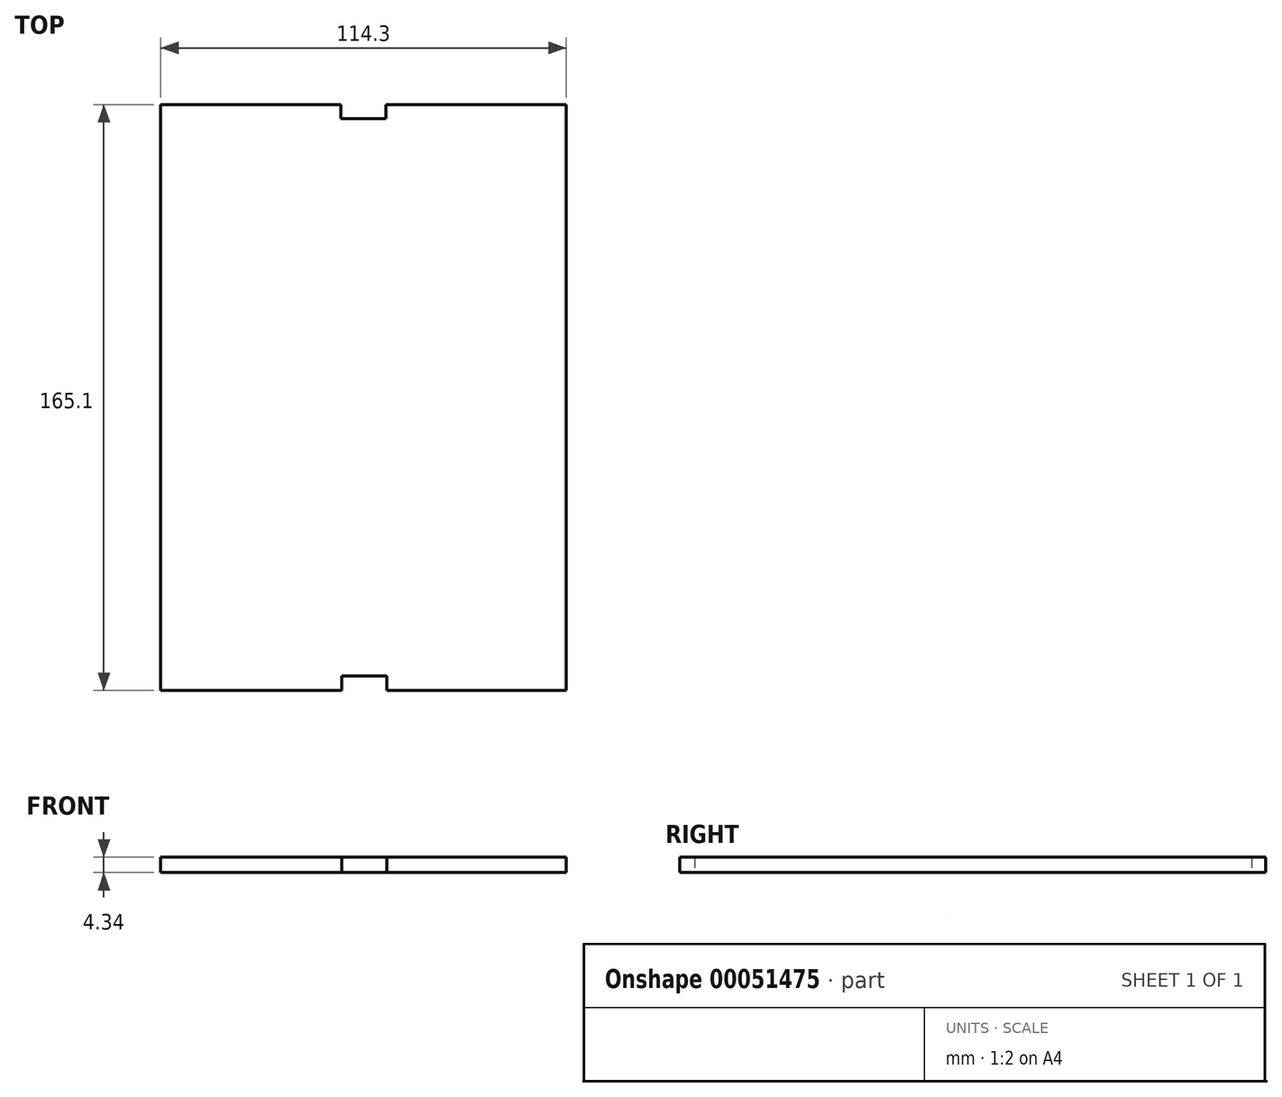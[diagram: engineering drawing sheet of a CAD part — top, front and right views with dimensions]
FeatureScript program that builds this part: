
annotation { "Feature Type Name" : "Feature", "Feature Type Description" : "" }
export const myFeature = defineFeature(function(context is Context, id is Id, definition is map)
    precondition{}
    {
        {
            var Q0;
            Q0=qCreatedBy(makeId("Top.planeOp"),FACE);
            var sketch = newSketch(context, id + "F0", { "sketchPlane" : qUnion([Q0])});
            skLineSegment(sketch, "E0.bottom", {"start": v(-56.26, 135.4) * mm, "end": v(58.04, 135.4) * mm});
            skLineSegment(sketch, "E0.top", {"start": v(-56.26, -29.7) * mm, "end": v(58.04, -29.7) * mm});
            skLineSegment(sketch, "E0.left", {"start": v(-56.26, 135.4) * mm, "end": v(-56.26, -29.7) * mm});
            skLineSegment(sketch, "E0.right", {"start": v(58.04, 135.4) * mm, "end": v(58.04, -29.7) * mm});
            skSolve(sketch);
        }
        {
            var Q0;
            Q0=qSketchRegion(id+"F0",true);
            extrude(context, id + "F1", {"entities" : qUnion([Q0]), "depth" : 4.34 * mm});
        }
        {
            var Q0;
            Q0=qCreatedBy(makeId("Top.planeOp"),FACE);
            var sketch = newSketch(context, id + "F2", { "sketchPlane" : qUnion([Q0])});
            skLineSegment(sketch, "E1.0", {"start": v(-5.46, 135.4) * mm, "end": v(-5.46, -29.37) * mm, "construction": true});
            skLineSegment(sketch, "E2", {"start": v(-57.24, 53.01) * mm, "end": v(58.42, 53.01) * mm, "construction": true});
            skPoint(sketch, "E2.startSnap0", {"position": v(-5.46, 53.01) * mm});
            skPoint(sketch, "E3.orphan", {"position": v(7.24, 131.05) * mm});
            skPoint(sketch, "E4.MirrorCS.start.orphan", {"position": v(-5.46, 131.05) * mm});
            skPoint(sketch, "E5.orphan", {"position": v(-5.46, 135.4) * mm});
            skPoint(sketch, "E6.MirrorCS.end.orphan", {"position": v(7.24, 135.4) * mm});
            skPoint(sketch, "E7.end.orphan", {"position": v(7.24, -25.02) * mm});
            skPoint(sketch, "E8.left.end.orphan", {"position": v(-5.46, -25.02) * mm});
            skLineSegment(sketch, "E9.left", {"start": v(-5.46, 131.05) * mm, "end": v(-5.46, 135.4) * mm});
            skLineSegment(sketch, "E9.right", {"start": v(7.24, 131.05) * mm, "end": v(7.24, 135.4) * mm});
            skPoint(sketch, "E10.orphan", {"position": v(7.24, -29.37) * mm});
            skPoint(sketch, "E11.start.orphan", {"position": v(0.89, 135.4) * mm});
            skPoint(sketch, "E12.trimOffspring.end.orphan", {"position": v(0.89, -29.37) * mm});
            skSolve(sketch);
        }
        {
            var Q0;
            Q0=qCreatedBy(makeId("Top.planeOp"),FACE);
            var sketch = newSketch(context, id + "F3", { "sketchPlane" : qUnion([Q0])});
            skLineSegment(sketch, "E13.top", {"start": v(-5.18, 131.6) * mm, "end": v(7.52, 131.6) * mm});
            skLineSegment(sketch, "E13.left", {"start": v(-5.18, 135.95) * mm, "end": v(-5.18, 131.6) * mm});
            skLineSegment(sketch, "E13.right", {"start": v(7.52, 135.95) * mm, "end": v(7.52, 131.6) * mm});
            skLineSegment(sketch, "E14.MirrorCS", {"start": v(-5.18, -29.92) * mm, "end": v(7.52, -29.92) * mm});
            skLineSegment(sketch, "E15.MirrorCS", {"start": v(-5.18, -29.92) * mm, "end": v(-5.18, -25.58) * mm});
            skLineSegment(sketch, "E16.MirrorCS", {"start": v(7.52, -29.92) * mm, "end": v(7.52, -25.58) * mm});
            skLineSegment(sketch, "E17.MirrorCS", {"start": v(-5.18, -25.58) * mm, "end": v(7.52, -25.58) * mm});
            skSolve(sketch);
        }
        {
            var Q0;
            Q0=qSketchRegion(id+"F3",true);
            extrude(context, id + "F4", {"entities" : qUnion([Q0]), "operationType" : NewBodyOperationType.REMOVE, "endBound" : BoundingType.THROUGH_ALL, "depth" : 4.34 * mm});
        }
        {
            var Q0;
            Q0=qCreatedBy(makeId("Top.planeOp"),FACE);
            var sketch = newSketch(context, id + "F5", { "sketchPlane" : qUnion([Q0])});
            skLineSegment(sketch, "E18.bottom", {"start": v(-5.45, 135.77) * mm, "end": v(7.25, 135.77) * mm});
            skLineSegment(sketch, "E18.top", {"start": v(-5.45, 131.43) * mm, "end": v(7.25, 131.43) * mm});
            skLineSegment(sketch, "E18.left", {"start": v(-5.45, 135.77) * mm, "end": v(-5.45, 131.43) * mm});
            skLineSegment(sketch, "E18.right", {"start": v(7.25, 135.77) * mm, "end": v(7.25, 131.43) * mm});
            skLineSegment(sketch, "E19", {"start": v(0, -29.45) * mm, "end": v(0, 143.66) * mm, "construction": true});
            skSolve(sketch);
        }
        {
            var Q0;
            Q0=qSketchRegion(id+"F5",true);
            extrude(context, id + "F6", {"entities" : qUnion([Q0]), "operationType" : NewBodyOperationType.REMOVE, "endBound" : BoundingType.THROUGH_ALL, "depth" : 25.4 * mm});
        }
    });
